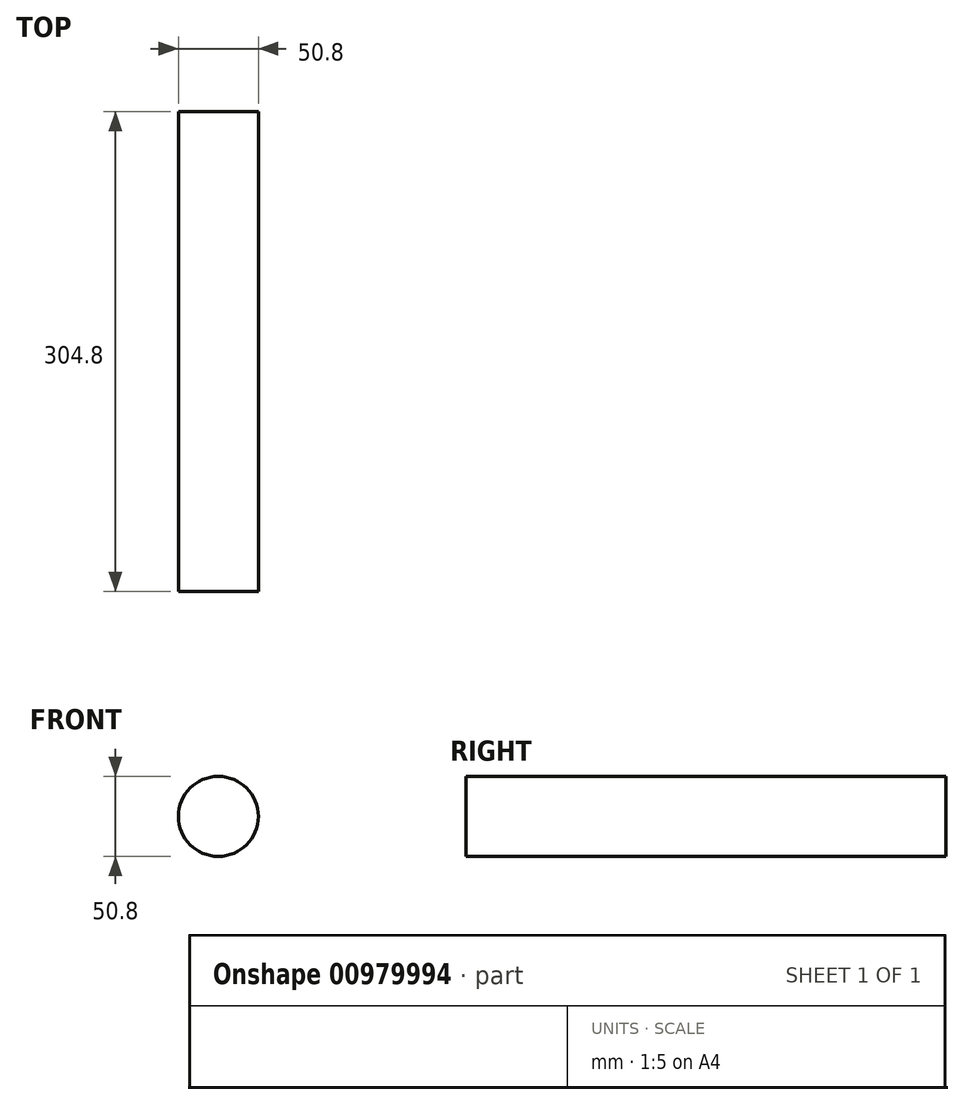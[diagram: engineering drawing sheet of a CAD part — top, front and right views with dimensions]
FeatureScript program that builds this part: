
annotation { "Feature Type Name" : "Feature", "Feature Type Description" : "" }
export const myFeature = defineFeature(function(context is Context, id is Id, definition is map)
    precondition{}
    {
        {
            var Q0;
            Q0=qCreatedBy(makeId("Front.planeOp"),FACE);
            var sketch = newSketch(context, id + "F0", { "sketchPlane" : qUnion([Q0])});
            skCircle(sketch, "E0", {"center": v(-30.33, 5.25) * mm, "radius": 25.4 * mm});
            skSolve(sketch);
        }
        {
            var Q0;
            Q0=makeQuery(id+"F0.imprint","IMPRINT",FACE,{"disambiguationData":[TD([[makeQuery(id+"F0.imprint","IMPRINT",EDGE,{"derivedFrom":sQuery(id+"F0.wireOp",EDGE,"E0")}),1.0]])]});
            extrude(context, id + "F1", {"entities" : qUnion([Q0]), "depth" : 304.8 * mm, "offsetDistance" : 25.4 * mm});
        }
    });
